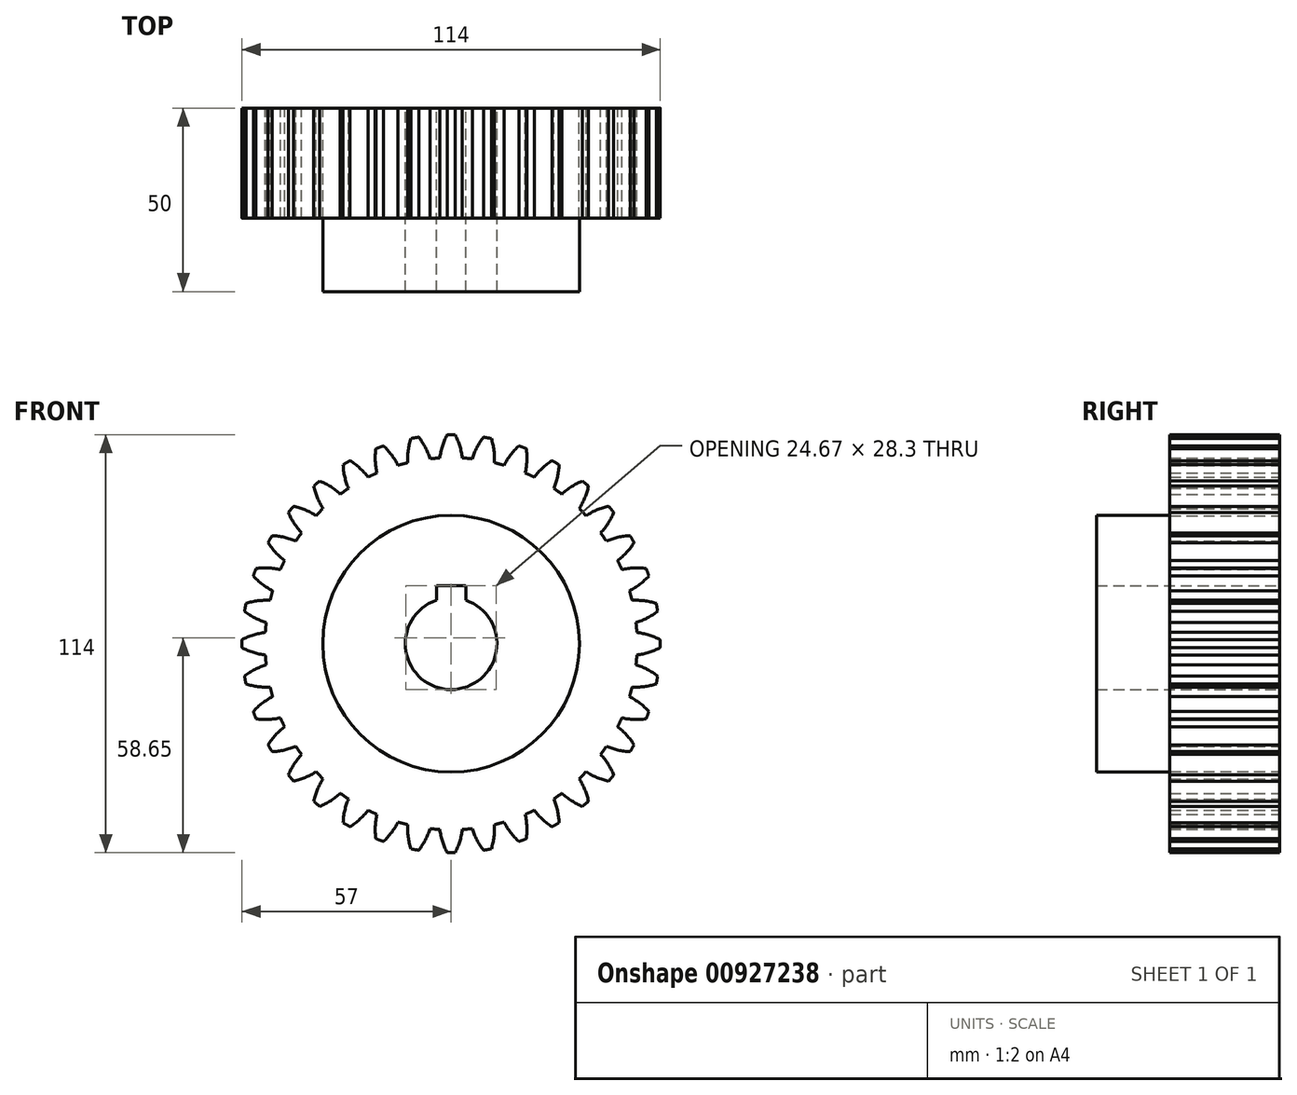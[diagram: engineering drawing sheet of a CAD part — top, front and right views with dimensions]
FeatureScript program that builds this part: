
annotation { "Feature Type Name" : "Feature", "Feature Type Description" : "" }
export const myFeature = defineFeature(function(context is Context, id is Id, definition is map)
    precondition{}
    {
        {
            var Q0;
            Q0=qCreatedBy(makeId("Front.planeOp"),FACE);
            var sketch = newSketch(context, id + "F0", { "sketchPlane" : qUnion([Q0])});
            skCircle(sketch, "E0", {"center": v(0, 0) * mm, "radius": 50.74 * mm});
            skSolve(sketch);
        }
        {
            var Q0;
            Q0=qSketchRegion(id+"F0",true);
            extrude(context, id + "F1", {"entities" : qUnion([Q0]), "depth" : 30 * mm, "offsetDistance" : 25 * mm});
        }
        {
            var Q0;
            Q0=qCreatedBy(makeId("Front.planeOp"),FACE);
            var sketch = newSketch(context, id + "F2", { "sketchPlane" : qUnion([Q0])});
            skArc(sketch, "E1", {"start": v(3.07, 50.65) * mm, "mid": v(0, 50.74) * mm, "end": v(-3.07, 50.65) * mm});
            skCircle(sketch, "E2", {"center": v(0, 0) * mm, "radius": 54 * mm, "construction": true});
            skArc(sketch, "E3", {"start": v(1.09, 56.99) * mm, "mid": v(0, 57) * mm, "end": v(-1.09, 56.99) * mm});
            skLineSegment(sketch, "E4", {"start": v(0, 0) * mm, "end": v(-2.36, 53.95) * mm, "construction": true});
            skLineSegment(sketch, "E5", {"start": v(-2.36, 53.95) * mm, "end": v(15.26, 48.4) * mm, "construction": true});
            skArc(sketch, "E6", {"start": v(-1.09, 56.99) * mm, "mid": v(-2.37, 53.9) * mm, "end": v(-3.07, 50.65) * mm});
            skArc(sketch, "E7.MirrorC", {"start": v(1.09, 56.99) * mm, "mid": v(2.37, 53.9) * mm, "end": v(3.07, 50.65) * mm});
            skLineSegment(sketch, "E8.MirrorCS", {"start": v(0, 0) * mm, "end": v(2.36, 53.95) * mm, "construction": true});
            skSolve(sketch);
        }
        {
            var Q0;
            Q0=qSketchRegion(id+"F2",true);
            var Q1;
            Q1=qConstructionFilter(qBodyType(qCreatedBy(id+"F2",EDGE),BodyType.WIRE),ConstructionObject.NO);
            var Q2;
            Q2=makeQuery(id+"F1.opExtrude","CAP_FACE",FACE,{"disambiguationData":[OSD([sQuery(id+"F0.wireOp",EDGE,"E0")])],"isStart":false});
            extrude(context, id + "F3", {"entities" : qUnion([Q0]), "surfaceEntities" : qUnion([Q1]), "endBound" : BoundingType.UP_TO_SURFACE, "depth" : 25 * mm, "endBoundEntityFace" : qUnion([Q2]), "offsetDistance" : 25 * mm});
        }
        {
            var Q0;
            Q0=makeQuery(id+"F3.opExtrude","SWEPT_BODY",BODY,{"disambiguationData":[OSD([sQuery(id+"F2.wireOp",EDGE,"E1"),sQuery(id+"F2.wireOp",EDGE,"E3"),sQuery(id+"F2.wireOp",EDGE,"E6"),sQuery(id+"F2.wireOp",EDGE,"E7.MirrorC")])]});
            var Q1;
            Q1=makeQuery(id+"F1.opExtrude","SWEPT_FACE",FACE,{"disambiguationData":[OSD([sQuery(id+"F0.wireOp",EDGE,"E0")])]});
            var Q2;
            Q2=makeQuery(id+"F1.opExtrude","SWEPT_BODY",BODY,{"disambiguationData":[OSD([sQuery(id+"F0.wireOp",EDGE,"E0")])]});
            circularPattern(context, id + "F4", {"operationType" : NewBodyOperationType.ADD, "entities" : qUnion([Q0]), "axis" : qUnion([Q1]), "angle" : 360 * degree, "instanceCount" : 36, "equalSpace" : true});
        }
        {
            var Q0;
            {var subQ0=makeQuery(id+"F3.opExtrude","CAP_FACE",FACE,{"disambiguationData":[OSD([sQuery(id+"F2.wireOp",EDGE,"27ea40b5-a951-41fe-b2b0-23b0c8f32f99"),sQuery(id+"F2.wireOp",EDGE,"g5MLrJZe-8DIj-dw4J-t7d3-wYIBbitemDrg"),sQuery(id+"F2.wireOp",EDGE,"a7c40835-1b0c-4428-97f4-bc1f4e4d2cdc0.MirrorCS"),sQuery(id+"F2.wireOp",EDGE,"71bf0348-7fa4-4463-ad31-61e3cc7938440.MirrorCS"),sQuery(id+"F2.wireOp",EDGE,"zAWKabWg-Dy0p-7wie-48dv-3QK1t6ZuBW5s"),sQuery(id+"F2.wireOp",EDGE,"8dd9605d-b27a-4633-b43e-2126b32a17ce.trimOffspring")])],"isStart":false});Q0=makeQuery(id+"F4.boolean.opBoolean","MERGE",FACE,{"derivedFrom":[makeQuery(id+"F1.opExtrude","CAP_FACE",FACE,{"disambiguationData":[OSD([sQuery(id+"F0.wireOp",EDGE,"E0")])],"isStart":false}),subQ0,makeQuery(id+"F4.opPattern","COPY",FACE,{"derivedFrom":subQ0,"instanceName":"1"}),makeQuery(id+"F4.opPattern","COPY",FACE,{"derivedFrom":subQ0,"instanceName":"2"}),makeQuery(id+"F4.opPattern","COPY",FACE,{"derivedFrom":subQ0,"instanceName":"3"}),makeQuery(id+"F4.opPattern","COPY",FACE,{"derivedFrom":subQ0,"instanceName":"4"}),makeQuery(id+"F4.opPattern","COPY",FACE,{"derivedFrom":subQ0,"instanceName":"5"}),makeQuery(id+"F4.opPattern","COPY",FACE,{"derivedFrom":subQ0,"instanceName":"6"}),makeQuery(id+"F4.opPattern","COPY",FACE,{"derivedFrom":subQ0,"instanceName":"7"}),makeQuery(id+"F4.opPattern","COPY",FACE,{"derivedFrom":subQ0,"instanceName":"8"}),makeQuery(id+"F4.opPattern","COPY",FACE,{"derivedFrom":subQ0,"instanceName":"9"}),makeQuery(id+"F4.opPattern","COPY",FACE,{"derivedFrom":subQ0,"instanceName":"10"}),makeQuery(id+"F4.opPattern","COPY",FACE,{"derivedFrom":subQ0,"instanceName":"11"}),makeQuery(id+"F4.opPattern","COPY",FACE,{"derivedFrom":subQ0,"instanceName":"12"}),makeQuery(id+"F4.opPattern","COPY",FACE,{"derivedFrom":subQ0,"instanceName":"13"}),makeQuery(id+"F4.opPattern","COPY",FACE,{"derivedFrom":subQ0,"instanceName":"14"}),makeQuery(id+"F4.opPattern","COPY",FACE,{"derivedFrom":subQ0,"instanceName":"15"}),makeQuery(id+"F4.opPattern","COPY",FACE,{"derivedFrom":subQ0,"instanceName":"16"}),makeQuery(id+"F4.opPattern","COPY",FACE,{"derivedFrom":subQ0,"instanceName":"17"}),makeQuery(id+"F4.opPattern","COPY",FACE,{"derivedFrom":subQ0,"instanceName":"18"}),makeQuery(id+"F4.opPattern","COPY",FACE,{"derivedFrom":subQ0,"instanceName":"19"}),makeQuery(id+"F4.opPattern","COPY",FACE,{"derivedFrom":subQ0,"instanceName":"20"}),makeQuery(id+"F4.opPattern","COPY",FACE,{"derivedFrom":subQ0,"instanceName":"21"}),makeQuery(id+"F4.opPattern","COPY",FACE,{"derivedFrom":subQ0,"instanceName":"22"}),makeQuery(id+"F4.opPattern","COPY",FACE,{"derivedFrom":subQ0,"instanceName":"23"}),makeQuery(id+"F4.opPattern","COPY",FACE,{"derivedFrom":subQ0,"instanceName":"24"}),makeQuery(id+"F4.opPattern","COPY",FACE,{"derivedFrom":subQ0,"instanceName":"25"}),makeQuery(id+"F4.opPattern","COPY",FACE,{"derivedFrom":subQ0,"instanceName":"26"}),makeQuery(id+"F4.opPattern","COPY",FACE,{"derivedFrom":subQ0,"instanceName":"27"}),makeQuery(id+"F4.opPattern","COPY",FACE,{"derivedFrom":subQ0,"instanceName":"28"}),makeQuery(id+"F4.opPattern","COPY",FACE,{"derivedFrom":subQ0,"instanceName":"29"}),makeQuery(id+"F4.opPattern","COPY",FACE,{"derivedFrom":subQ0,"instanceName":"30"}),makeQuery(id+"F4.opPattern","COPY",FACE,{"derivedFrom":subQ0,"instanceName":"31"}),makeQuery(id+"F4.opPattern","COPY",FACE,{"derivedFrom":subQ0,"instanceName":"32"}),makeQuery(id+"F4.opPattern","COPY",FACE,{"derivedFrom":subQ0,"instanceName":"33"}),makeQuery(id+"F4.opPattern","COPY",FACE,{"derivedFrom":subQ0,"instanceName":"34"}),makeQuery(id+"F4.opPattern","COPY",FACE,{"derivedFrom":subQ0,"instanceName":"35"}),makeQuery(id+"F4.opPattern","COPY",FACE,{"derivedFrom":subQ0,"instanceName":"36"}),makeQuery(id+"F4.opPattern","COPY",FACE,{"derivedFrom":subQ0,"instanceName":"37"}),makeQuery(id+"F4.opPattern","COPY",FACE,{"derivedFrom":subQ0,"instanceName":"38"}),makeQuery(id+"F4.opPattern","COPY",FACE,{"derivedFrom":subQ0,"instanceName":"39"}),makeQuery(id+"F4.opPattern","COPY",FACE,{"derivedFrom":subQ0,"instanceName":"40"}),makeQuery(id+"F4.opPattern","COPY",FACE,{"derivedFrom":subQ0,"instanceName":"41"}),makeQuery(id+"F4.opPattern","COPY",FACE,{"derivedFrom":subQ0,"instanceName":"42"}),makeQuery(id+"F4.opPattern","COPY",FACE,{"derivedFrom":subQ0,"instanceName":"43"}),makeQuery(id+"F4.opPattern","COPY",FACE,{"derivedFrom":subQ0,"instanceName":"44"}),makeQuery(id+"F4.opPattern","COPY",FACE,{"derivedFrom":subQ0,"instanceName":"45"}),makeQuery(id+"F4.opPattern","COPY",FACE,{"derivedFrom":subQ0,"instanceName":"46"}),makeQuery(id+"F4.opPattern","COPY",FACE,{"derivedFrom":subQ0,"instanceName":"47"}),makeQuery(id+"F4.opPattern","COPY",FACE,{"derivedFrom":subQ0,"instanceName":"48"}),makeQuery(id+"F4.opPattern","COPY",FACE,{"derivedFrom":subQ0,"instanceName":"49"}),makeQuery(id+"F4.opPattern","COPY",FACE,{"derivedFrom":subQ0,"instanceName":"50"}),makeQuery(id+"F4.opPattern","COPY",FACE,{"derivedFrom":subQ0,"instanceName":"51"}),makeQuery(id+"F4.opPattern","COPY",FACE,{"derivedFrom":subQ0,"instanceName":"52"}),makeQuery(id+"F4.opPattern","COPY",FACE,{"derivedFrom":subQ0,"instanceName":"53"}),makeQuery(id+"F4.opPattern","COPY",FACE,{"derivedFrom":subQ0,"instanceName":"54"}),makeQuery(id+"F4.opPattern","COPY",FACE,{"derivedFrom":subQ0,"instanceName":"55"}),makeQuery(id+"F4.opPattern","COPY",FACE,{"derivedFrom":subQ0,"instanceName":"56"}),makeQuery(id+"F4.opPattern","COPY",FACE,{"derivedFrom":subQ0,"instanceName":"57"}),makeQuery(id+"F4.opPattern","COPY",FACE,{"derivedFrom":subQ0,"instanceName":"58"}),makeQuery(id+"F4.opPattern","COPY",FACE,{"derivedFrom":subQ0,"instanceName":"59"}),makeQuery(id+"F4.opPattern","COPY",FACE,{"derivedFrom":subQ0,"instanceName":"60"}),makeQuery(id+"F4.opPattern","COPY",FACE,{"derivedFrom":subQ0,"instanceName":"61"}),makeQuery(id+"F4.opPattern","COPY",FACE,{"derivedFrom":subQ0,"instanceName":"62"}),makeQuery(id+"F4.opPattern","COPY",FACE,{"derivedFrom":subQ0,"instanceName":"63"}),makeQuery(id+"F4.opPattern","COPY",FACE,{"derivedFrom":subQ0,"instanceName":"64"}),makeQuery(id+"F4.opPattern","COPY",FACE,{"derivedFrom":subQ0,"instanceName":"65"}),makeQuery(id+"F4.opPattern","COPY",FACE,{"derivedFrom":subQ0,"instanceName":"66"}),makeQuery(id+"F4.opPattern","COPY",FACE,{"derivedFrom":subQ0,"instanceName":"67"}),makeQuery(id+"F4.opPattern","COPY",FACE,{"derivedFrom":subQ0,"instanceName":"68"}),makeQuery(id+"F4.opPattern","COPY",FACE,{"derivedFrom":subQ0,"instanceName":"69"}),makeQuery(id+"F4.opPattern","COPY",FACE,{"derivedFrom":subQ0,"instanceName":"70"}),makeQuery(id+"F4.opPattern","COPY",FACE,{"derivedFrom":subQ0,"instanceName":"71"}),makeQuery(id+"F4.opPattern","COPY",FACE,{"derivedFrom":subQ0,"instanceName":"72"}),makeQuery(id+"F4.opPattern","COPY",FACE,{"derivedFrom":subQ0,"instanceName":"73"}),makeQuery(id+"F4.opPattern","COPY",FACE,{"derivedFrom":subQ0,"instanceName":"74"})]});}
            var sketch = newSketch(context, id + "F5", { "sketchPlane" : qUnion([Q0])});
            skCircle(sketch, "E9", {"center": v(0, 0) * mm, "radius": 35 * mm});
            skSolve(sketch);
        }
        {
            var Q0;
            Q0=qSketchRegion(id+"F5",true);
            extrude(context, id + "F6", {"entities" : qUnion([Q0]), "operationType" : NewBodyOperationType.ADD, "depth" : 20 * mm, "offsetDistance" : 25 * mm});
        }
        {
            var Q0;
            Q0=qCreatedBy(makeId("Front.planeOp"),FACE);
            var sketch = newSketch(context, id + "F7", { "sketchPlane" : qUnion([Q0])});
            skLineSegment(sketch, "E10.top", {"start": v(-4, 15.8) * mm, "end": v(4, 15.8) * mm});
            skLineSegment(sketch, "E10.left", {"start": v(-4, 11.84) * mm, "end": v(-4, 15.8) * mm});
            skLineSegment(sketch, "E10.right", {"start": v(4, 11.84) * mm, "end": v(4, 11.84) * mm});
            skPoint(sketch, "E11.orphan", {"position": v(-4, 0) * mm});
            skLineSegment(sketch, "E12", {"start": v(4, 11.84) * mm, "end": v(4, 15.8) * mm});
            skArc(sketch, "E13", {"start": v(-4, 11.84) * mm, "mid": v(0, -12.5) * mm, "end": v(4, 11.84) * mm});
            skArc(sketch, "E14", {"start": v(4, 11.84) * mm, "mid": v(0, 12.5) * mm, "end": v(-4, 11.84) * mm, "construction": true});
            skSolve(sketch);
        }
        {
            var Q0;
            Q0=qSketchRegion(id+"F7",true);
            extrude(context, id + "F8", {"entities" : qUnion([Q0]), "operationType" : NewBodyOperationType.REMOVE, "endBound" : BoundingType.THROUGH_ALL, "depth" : 25 * mm, "offsetDistance" : 25 * mm});
        }
        {
            var Q0;
            Q0=makeQuery(id+"F8.boolean.opBoolean","COPY",EDGE,{"derivedFrom":makeQuery(id+"F8.opExtrude","SWEPT_EDGE",EDGE,{"disambiguationData":[OSD([sQuery(id+"F7.wireOp",EDGE,"E10.top"),sQuery(id+"F7.wireOp",EDGE,"E10.left")])]})});
            var Q1;
            Q1=makeQuery(id+"F8.boolean.opBoolean","COPY",EDGE,{"derivedFrom":makeQuery(id+"F8.opExtrude","SWEPT_EDGE",EDGE,{"disambiguationData":[OSD([sQuery(id+"F7.wireOp",EDGE,"E10.top"),sQuery(id+"F7.wireOp",EDGE,"E12")])]})});
            fillet(context, id + "F9", {"entities" : qUnion([Q0, Q1]), "radius" : 0.2 * mm, "tangentPropagation" : true, "allowEdgeOverflow" : false});
        }
    });
